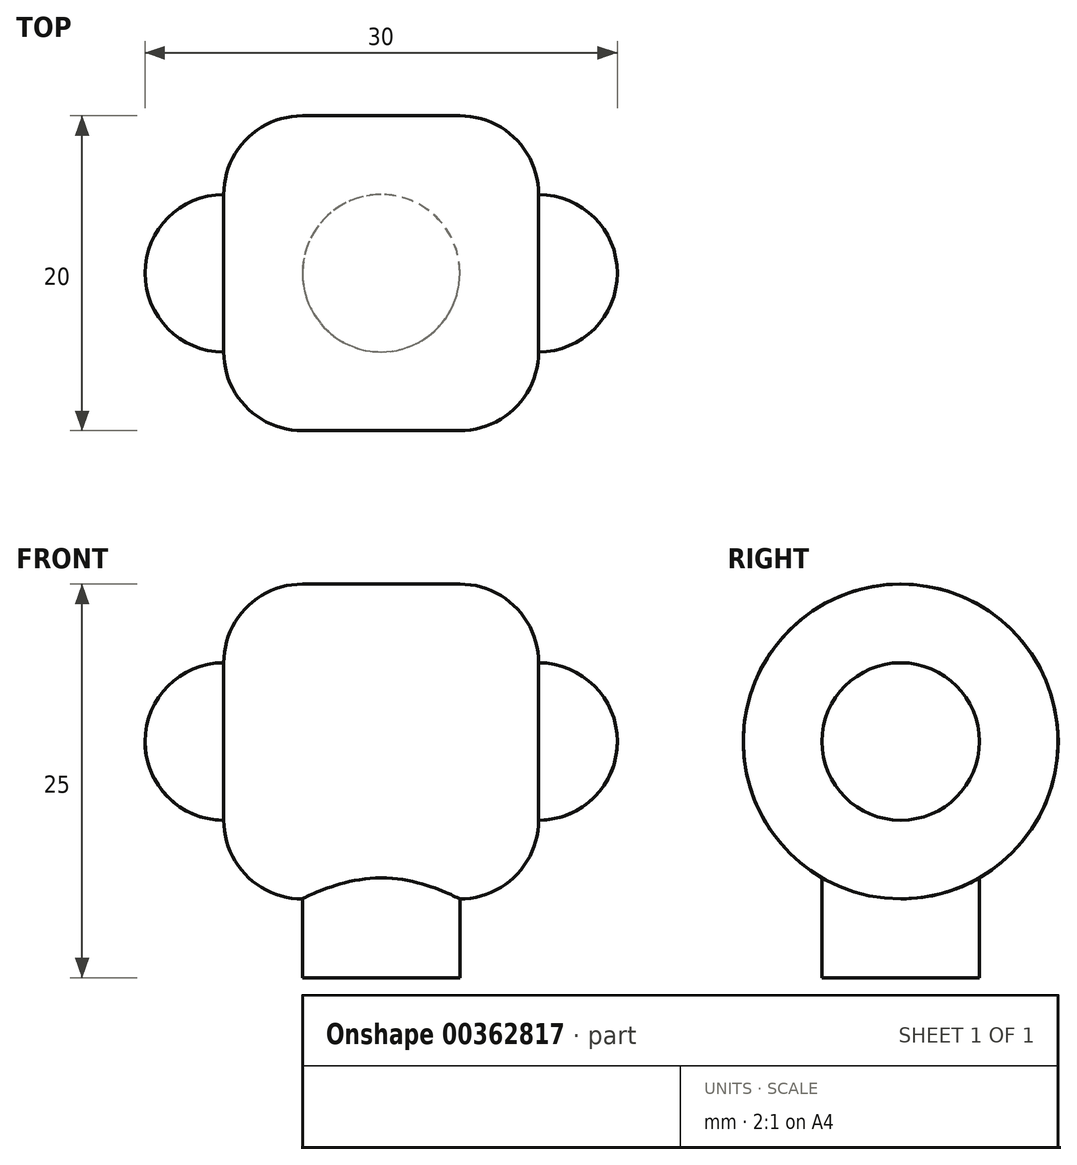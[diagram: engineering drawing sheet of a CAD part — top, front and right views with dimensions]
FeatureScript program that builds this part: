
annotation { "Feature Type Name" : "Feature", "Feature Type Description" : "" }
export const myFeature = defineFeature(function(context is Context, id is Id, definition is map)
    precondition{}
    {
        {
            var Q0;
            Q0=qCreatedBy(makeId("Right.planeOp"),FACE);
            var sketch = newSketch(context, id + "F0", { "sketchPlane" : qUnion([Q0])});
            skCircle(sketch, "E0", {"center": v(0, 16.47) * mm, "radius": 5 * mm});
            skCircle(sketch, "E1", {"center": v(0, 16.47) * mm, "radius": 10 * mm});
            skLineSegment(sketch, "E2.bottom", {"start": v(-5, 16.47) * mm, "end": v(5, 16.47) * mm});
            skLineSegment(sketch, "E2.top", {"start": v(-5, 1.47) * mm, "end": v(5, 1.47) * mm});
            skLineSegment(sketch, "E2.left", {"start": v(-5, 16.47) * mm, "end": v(-5, 1.47) * mm});
            skLineSegment(sketch, "E2.right", {"start": v(5, 16.47) * mm, "end": v(5, 1.47) * mm});
            skSolve(sketch);
        }
        {
            var Q0;
            Q0=makeQuery(id+"F0.imprint","IMPRINT",FACE,{"disambiguationData":[TD([[makeQuery(id+"F0.imprint","IMPRINT",EDGE,{"derivedFrom":sQuery(id+"F0.wireOp",EDGE,"E0")}),1.0]])]});
            extrude(context, id + "F1", {"entities" : qUnion([Q0]), "depth" : 15 * mm, "hasSecondDirection" : true, "secondDirectionOppositeDirection" : true, "secondDirectionDepth" : 15 * mm});
        }
        {
            var Q0;
            {var subQ0=sQuery(id+"F0.wireOp",EDGE,"E2.left");var subQ6=sQuery(id+"F0.wireOp",EDGE,"E1");var subQ7=makeQuery(id+"F0.imprint","INTERSECT",VERTEX,{"derivedFrom":[subQ6,subQ0]});Q0=makeQuery(id+"F0.imprint","IMPRINT",FACE,{"disambiguationData":[TD([[makeQuery(id+"F0.imprint","IMPRINT",EDGE,{"disambiguationData":[TD([[subQ7,1.0]])],"derivedFrom":subQ6}),1.0]])]});}
            var Q1;
            {var subQ0=sQuery(id+"F0.wireOp",EDGE,"E2.left");var subQ6=sQuery(id+"F0.wireOp",EDGE,"E1");var subQ7=makeQuery(id+"F0.imprint","INTERSECT",VERTEX,{"derivedFrom":[subQ6,subQ0]});Q1=makeQuery(id+"F0.imprint","IMPRINT",FACE,{"disambiguationData":[TD([[makeQuery(id+"F0.imprint","IMPRINT",EDGE,{"disambiguationData":[TD([[subQ7,-1.0]])],"derivedFrom":subQ6}),1.0]])]});}
            extrude(context, id + "F2", {"entities" : qUnion([Q0, Q1]), "operationType" : NewBodyOperationType.ADD, "depth" : 10 * mm, "hasSecondDirection" : true, "secondDirectionOppositeDirection" : true, "secondDirectionDepth" : 10 * mm});
        }
        {
            var Q0;
            {var subQ5=sQuery(id+"F0.wireOp",EDGE,"E2.top");Q0=makeQuery(id+"F0.imprint","IMPRINT",FACE,{"disambiguationData":[TD([[makeQuery(id+"F0.imprint","IMPRINT",EDGE,{"derivedFrom":subQ5}),1.0]])]});}
            extrude(context, id + "F3", {"entities" : qUnion([Q0]), "operationType" : NewBodyOperationType.ADD, "depth" : 5 * mm, "hasSecondDirection" : true, "secondDirectionOppositeDirection" : true, "secondDirectionDepth" : 5 * mm});
        }
        {
            var Q0;
            Q0=makeQuery(id+"F1.opExtrude","CAP_EDGE",EDGE,{"disambiguationData":[OSD([sQuery(id+"F0.wireOp",EDGE,"E0")])],"isStart":false});
            var Q1;
            Q1=makeQuery(id+"F1.opExtrude","CAP_EDGE",EDGE,{"disambiguationData":[OSD([sQuery(id+"F0.wireOp",EDGE,"E0")])],"isStart":true});
            fillet(context, id + "F4", {"entities" : qUnion([Q0, Q1]), "radius" : 5 * mm, "tangentPropagation" : true, "allowEdgeOverflow" : false});
        }
        {
            var Q0;
            Q0=makeQuery(id+"F2.opExtrude","CAP_EDGE",EDGE,{"disambiguationData":[OSD([sQuery(id+"F0.wireOp",EDGE,"E1")])],"isStart":true});
            var Q1;
            Q1=makeQuery(id+"F2.opExtrude","CAP_EDGE",EDGE,{"disambiguationData":[OSD([sQuery(id+"F0.wireOp",EDGE,"E2.right")])],"isStart":true});
            var Q2;
            Q2=makeQuery(id+"F2.opExtrude","CAP_EDGE",EDGE,{"disambiguationData":[OSD([sQuery(id+"F0.wireOp",EDGE,"E2.left")])],"isStart":true});
            var Q3;
            Q3=makeQuery(id+"F2.opExtrude","CAP_EDGE",EDGE,{"disambiguationData":[OSD([sQuery(id+"F0.wireOp",EDGE,"E2.right")])],"isStart":false});
            var Q4;
            Q4=makeQuery(id+"F2.opExtrude","CAP_EDGE",EDGE,{"disambiguationData":[OSD([sQuery(id+"F0.wireOp",EDGE,"E1")])],"isStart":false});
            var Q5;
            Q5=makeQuery(id+"F2.opExtrude","CAP_EDGE",EDGE,{"disambiguationData":[OSD([sQuery(id+"F0.wireOp",EDGE,"E2.left")])],"isStart":false});
            var Q6;
            Q6=makeQuery(id+"F3.opExtrude","CAP_EDGE",EDGE,{"disambiguationData":[OSD([sQuery(id+"F0.wireOp",EDGE,"E2.right")])],"isStart":true});
            var Q7;
            Q7=makeQuery(id+"F3.opExtrude","CAP_EDGE",EDGE,{"disambiguationData":[OSD([sQuery(id+"F0.wireOp",EDGE,"E2.right")])],"isStart":false});
            var Q8;
            Q8=makeQuery(id+"F3.opExtrude","CAP_EDGE",EDGE,{"disambiguationData":[OSD([sQuery(id+"F0.wireOp",EDGE,"E2.left")])],"isStart":false});
            var Q9;
            Q9=makeQuery(id+"F3.opExtrude","CAP_EDGE",EDGE,{"disambiguationData":[OSD([sQuery(id+"F0.wireOp",EDGE,"E2.left")])],"isStart":true});
            fillet(context, id + "F5", {"entities" : qUnion([Q0, Q1, Q2, Q3, Q4, Q5, Q6, Q7, Q8, Q9]), "radius" : 5 * mm, "tangentPropagation" : true, "allowEdgeOverflow" : false});
        }
    });
